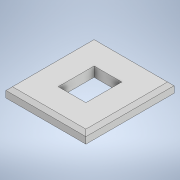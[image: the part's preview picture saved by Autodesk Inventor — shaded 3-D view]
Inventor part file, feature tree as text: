
AUTODESK INVENTOR PART (.ipt)
format: ipt  version: 2021 (Build 250183000, 183)  size: 106,496 bytes
history: native  units: in
note: dims shown in document units (in); Inventor stores cm internally (conversion verified against a paired STEP export)
features: extrude x1, chamfer x1, sketch x1
ambient origin geometry x8: Origin, YZ Plane, XZ Plane, XY Plane, X Axis, Y Axis, Z Axis, Center Point
bodies: Solid1 (feature_tree)
feature tree (3):
  extrude  "Extrusion1"  Depth=1.063in TaperAngle=45.0deg
  chamfer  "Chamfer1"  Distance=0.3346in
  sketch  "Sketch1"  dims[d8=0.1181in d9=0.0in d10=0.0394in d11=0.0787in d12=45.0deg d13=0.3346in d14=0.4331in d16=0.315in d17=0.9646in d18=1.063in]
